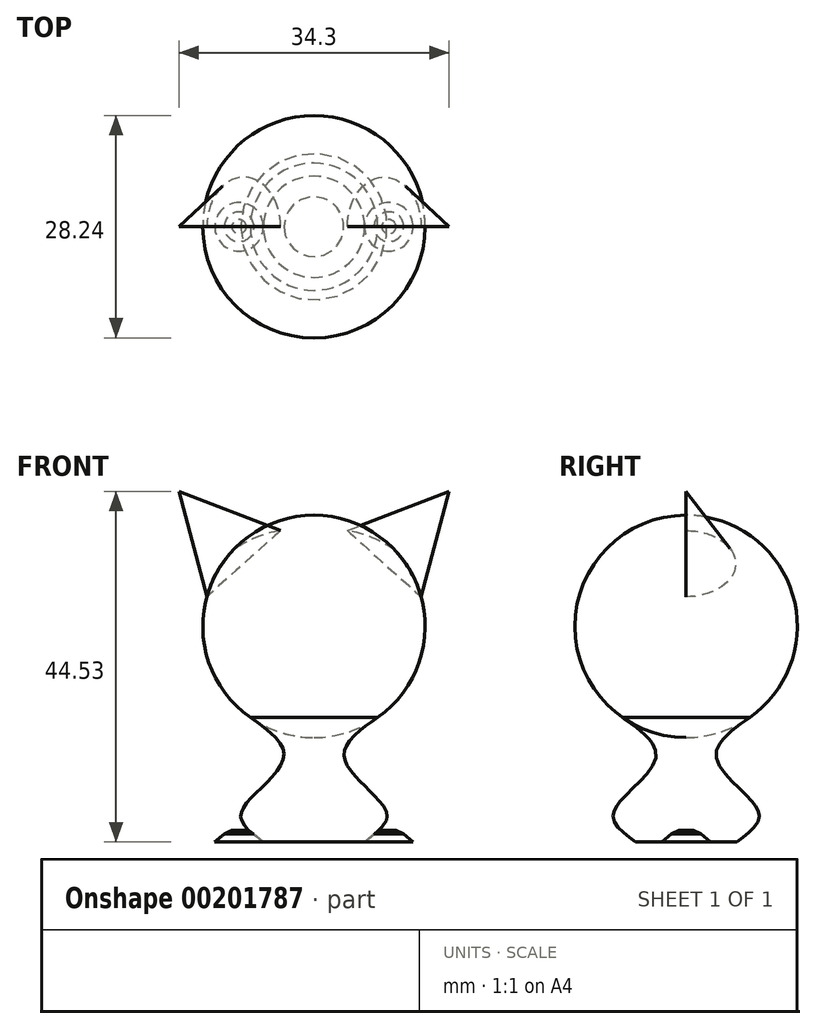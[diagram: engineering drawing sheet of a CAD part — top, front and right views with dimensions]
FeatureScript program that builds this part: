
annotation { "Feature Type Name" : "Feature", "Feature Type Description" : "" }
export const myFeature = defineFeature(function(context is Context, id is Id, definition is map)
    precondition{}
    {
        {
            var Q0;
            Q0=qCreatedBy(makeId("Front.planeOp"),FACE);
            var sketch = newSketch(context, id + "F0", { "sketchPlane" : qUnion([Q0])});
            skCircle(sketch, "E0", {"center": v(0, 0) * mm, "radius": 14.12 * mm});
            skLineSegment(sketch, "E1", {"start": v(-13.61, 3.77) * mm, "end": v(-17.15, 17.15) * mm});
            skLineSegment(sketch, "E2", {"start": v(-17.15, 17.15) * mm, "end": v(-6.52, 12.53) * mm});
            skLineSegment(sketch, "E3", {"start": v(-17.15, 17.15) * mm, "end": v(-10.37, 9.59) * mm});
            skLineSegment(sketch, "E4.MirrorCS", {"start": v(13.61, 3.77) * mm, "end": v(17.15, 17.15) * mm});
            skLineSegment(sketch, "E5.MirrorCS", {"start": v(17.15, 17.15) * mm, "end": v(10.37, 9.59) * mm});
            skLineSegment(sketch, "E6.MirrorCS", {"start": v(17.15, 17.15) * mm, "end": v(6.52, 12.53) * mm});
            skLineSegment(sketch, "E7", {"start": v(0, 14.12) * mm, "end": v(0, -14.12) * mm});
            skFitSpline(sketch, "E8", {"points": [v(-8.08, -11.58) * mm, v(-3.8, -16.2) * mm, v(-7.14, -20.96) * mm, v(-9.29, -24.29) * mm, v(-6.43, -27.38) * mm], "startDerivative": vector(22.65, -15.96) * mm, "endDerivative": vector(17.83, -13.3) * mm});
            skLineSegment(sketch, "E9", {"start": v(-6.43, -27.38) * mm, "end": v(0, -27.38) * mm});
            skLineSegment(sketch, "E10", {"start": v(0, -27.38) * mm, "end": v(0, -14.12) * mm});
            skLineSegment(sketch, "E11", {"start": v(-7.8, -26.37) * mm, "end": v(-9.1, -25.9) * mm});
            skLineSegment(sketch, "E12", {"start": v(-9.1, -25.9) * mm, "end": v(-10.42, -25.9) * mm});
            skLineSegment(sketch, "E13", {"start": v(-10.42, -25.9) * mm, "end": v(-11.4, -26.37) * mm});
            skLineSegment(sketch, "E14", {"start": v(-11.4, -26.37) * mm, "end": v(-12.6, -27.38) * mm});
            skLineSegment(sketch, "E15", {"start": v(-12.6, -27.38) * mm, "end": v(-6.43, -27.38) * mm});
            skLineSegment(sketch, "E16", {"start": v(-9.51, -27.38) * mm, "end": v(-9.51, -25.9) * mm});
            skFitSpline(sketch, "E17.MirrorCS", {"points": [v(8.08, -11.58) * mm, v(3.8, -16.2) * mm, v(7.14, -20.96) * mm, v(9.29, -24.29) * mm, v(6.43, -27.38) * mm], "startDerivative": vector(-22.65, -15.96) * mm, "endDerivative": vector(-17.83, -13.3) * mm});
            skLineSegment(sketch, "E18.MirrorCS", {"start": v(12.6, -27.38) * mm, "end": v(6.43, -27.38) * mm});
            skLineSegment(sketch, "E19.MirrorCS", {"start": v(7.8, -26.37) * mm, "end": v(9.1, -25.9) * mm});
            skLineSegment(sketch, "E20.MirrorCS", {"start": v(6.43, -27.38) * mm, "end": v(0, -27.38) * mm});
            skLineSegment(sketch, "E21.MirrorCS", {"start": v(9.1, -25.9) * mm, "end": v(10.42, -25.9) * mm});
            skLineSegment(sketch, "E22.MirrorCS", {"start": v(10.42, -25.9) * mm, "end": v(11.4, -26.37) * mm});
            skLineSegment(sketch, "E23.MirrorCS", {"start": v(11.4, -26.37) * mm, "end": v(12.6, -27.38) * mm});
            skLineSegment(sketch, "E24.MirrorCS", {"start": v(9.51, -27.38) * mm, "end": v(9.51, -25.9) * mm});
            skSolve(sketch);
        }
        {
            var Q0;
            {var subQ3=sQuery(id+"F0.wireOp",EDGE,"E13");Q0=makeQuery(id+"F0.imprint","IMPRINT",FACE,{"disambiguationData":[TD([[makeQuery(id+"F0.imprint","IMPRINT",EDGE,{"derivedFrom":subQ3}),1.0]])]});}
            var Q1;
            Q1=sQuery(id+"F0.wireOp",EDGE,"E16");
            revolve(context, id + "F1", {"entities" : qUnion([Q0]), "axis" : qUnion([Q1]), "revolveType" : RevolveType.FULL});
        }
        {
            var Q0;
            {var subQ3=sQuery(id+"F0.wireOp",EDGE,"E22.MirrorCS");Q0=makeQuery(id+"F0.imprint","IMPRINT",FACE,{"disambiguationData":[TD([[makeQuery(id+"F0.imprint","IMPRINT",EDGE,{"derivedFrom":subQ3}),-1.0]])]});}
            var Q1;
            Q1=sQuery(id+"F0.wireOp",EDGE,"E24.MirrorCS");
            revolve(context, id + "F2", {"entities" : qUnion([Q0]), "axis" : qUnion([Q1]), "revolveType" : RevolveType.FULL});
        }
        {
            var Q0;
            {var subQ2=sQuery(id+"F0.wireOp",EDGE,"E8");Q0=makeQuery(id+"F0.imprint","IMPRINT",FACE,{"disambiguationData":[TD([[makeQuery(id+"F0.imprint","IMPRINT",EDGE,{"derivedFrom":subQ2}),1.0]])]});}
            var Q1;
            Q1=sQuery(id+"F0.wireOp",EDGE,"E10");
            revolve(context, id + "F3", {"entities" : qUnion([Q0]), "axis" : qUnion([Q1]), "revolveType" : RevolveType.FULL});
        }
        {
            var Q0;
            {var subQ2=sQuery(id+"F0.wireOp",EDGE,"E7");Q0=makeQuery(id+"F0.imprint","IMPRINT",FACE,{"disambiguationData":[TD([[makeQuery(id+"F0.imprint","IMPRINT",EDGE,{"derivedFrom":subQ2}),1.0]])]});}
            var Q1;
            Q1=sQuery(id+"F0.wireOp",EDGE,"E7");
            revolve(context, id + "F4", {"entities" : qUnion([Q0]), "axis" : qUnion([Q1]), "revolveType" : RevolveType.FULL});
        }
        {
            var Q0;
            {var subQ0=sQuery(id+"F0.wireOp",EDGE,"E1");Q0=makeQuery(id+"F0.imprint","IMPRINT",FACE,{"disambiguationData":[TD([[makeQuery(id+"F0.imprint","IMPRINT",EDGE,{"derivedFrom":subQ0}),-1.0]])]});}
            var Q1;
            Q1=sQuery(id+"F0.wireOp",EDGE,"E3");
            revolve(context, id + "F5", {"entities" : qUnion([Q0]), "axis" : qUnion([Q1]), "revolveType" : RevolveType.ONE_DIRECTION, "angle" : 180 * degree});
        }
        {
            var Q0;
            {var subQ0=sQuery(id+"F0.wireOp",EDGE,"E4.MirrorCS");Q0=makeQuery(id+"F0.imprint","IMPRINT",FACE,{"disambiguationData":[TD([[makeQuery(id+"F0.imprint","IMPRINT",EDGE,{"derivedFrom":subQ0}),1.0]])]});}
            var Q1;
            Q1=sQuery(id+"F0.wireOp",EDGE,"E5.MirrorCS");
            revolve(context, id + "F6", {"entities" : qUnion([Q0]), "axis" : qUnion([Q1]), "revolveType" : RevolveType.ONE_DIRECTION, "oppositeDirection" : true, "angle" : 180 * degree});
        }
    });
